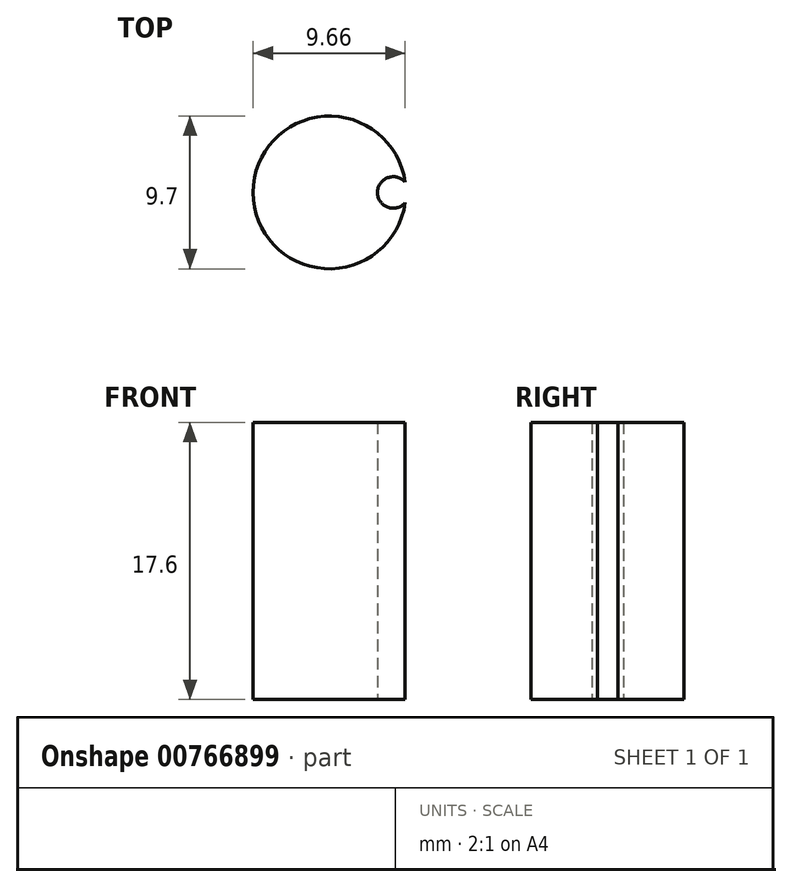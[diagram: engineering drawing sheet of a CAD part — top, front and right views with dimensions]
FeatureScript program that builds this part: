
annotation { "Feature Type Name" : "Feature", "Feature Type Description" : "" }
export const myFeature = defineFeature(function(context is Context, id is Id, definition is map)
    precondition{}
    {
        {
            var Q0;
            Q0=qCreatedBy(makeId("Top.planeOp"),FACE);
            var sketch = newSketch(context, id + "F0", { "sketchPlane" : qUnion([Q0])});
            skLineSegment(sketch, "E0", {"start": v(0, 0) * mm, "end": v(4.05, 0) * mm});
            skCircle(sketch, "E1", {"center": v(4.05, 0) * mm, "radius": 4.85 * mm});
            skLineSegment(sketch, "E2", {"start": v(0, 0) * mm, "end": v(0, -9.22) * mm});
            skCircle(sketch, "E3.MirrorC", {"center": v(-4.05, 0) * mm, "radius": 4.85 * mm});
            skCircle(sketch, "E4", {"center": v(0, 0) * mm, "radius": 1 * mm});
            skSolve(sketch);
        }
        {
            var Q0;
            {var subQ0=sQuery(id+"F0.wireOp",EDGE,"E3.MirrorC");var subQ1=sQuery(id+"F0.wireOp",EDGE,"E1");var subQ2=makeQuery(id+"F0.imprint","INTERSECT",VERTEX,{"derivedFrom":[subQ1,subQ0]});Q0=makeQuery(id+"F0.imprint","IMPRINT",FACE,{"disambiguationData":[TD([[makeQuery(id+"F0.imprint","IMPRINT",EDGE,{"disambiguationData":[TD([[subQ2,-1.0]])],"derivedFrom":subQ1}),-1.0]])]});}
            var Q1;
            {var subQ0=sQuery(id+"F0.wireOp",EDGE,"E3.MirrorC");var subQ1=sQuery(id+"F0.wireOp",EDGE,"E1");var subQ7=makeQuery(id+"F0.imprint","INTERSECT",VERTEX,{"derivedFrom":[subQ1,subQ0]});Q1=makeQuery(id+"F0.imprint","IMPRINT",FACE,{"disambiguationData":[TD([[makeQuery(id+"F0.imprint","IMPRINT",EDGE,{"disambiguationData":[TD([[subQ7,-1.0]])],"derivedFrom":subQ0}),1.0]])]});}
            var Q2;
            {var subQ1=sQuery(id+"F0.wireOp",EDGE,"E2");var subQ3=sQuery(id+"F0.wireOp",EDGE,"E4");var subQ4=makeQuery(id+"F0.imprint","INTERSECT",VERTEX,{"derivedFrom":[subQ1,subQ3]});Q2=makeQuery(id+"F0.imprint","IMPRINT",FACE,{"disambiguationData":[TD([[makeQuery(id+"F0.imprint","IMPRINT",EDGE,{"disambiguationData":[TD([[subQ4,-1.0]])],"derivedFrom":subQ3}),-1.0]])]});}
            var Q3;
            {var subQ0=sQuery(id+"F0.wireOp",EDGE,"E4");var subQ1=sQuery(id+"F0.wireOp",EDGE,"E1");var subQ2=makeQuery(id+"F0.imprint","INTERSECT",VERTEX,{"disambiguationData":[OD(1.0)],"derivedFrom":[subQ1,subQ0]});Q3=makeQuery(id+"F0.imprint","IMPRINT",FACE,{"disambiguationData":[TD([[makeQuery(id+"F0.imprint","IMPRINT",EDGE,{"disambiguationData":[TD([[subQ2,-1.0]])],"derivedFrom":subQ0}),-1.0]])]});}
            var Q4;
            {var subQ0=sQuery(id+"F0.wireOp",EDGE,"E3.MirrorC");var subQ1=sQuery(id+"F0.wireOp",EDGE,"E1");var subQ2=makeQuery(id+"F0.imprint","INTERSECT",VERTEX,{"derivedFrom":[subQ1,subQ0]});Q4=makeQuery(id+"F0.imprint","IMPRINT",FACE,{"disambiguationData":[TD([[makeQuery(id+"F0.imprint","IMPRINT",EDGE,{"disambiguationData":[TD([[subQ2,-1.0]])],"derivedFrom":subQ1}),1.0]])]});}
            extrude(context, id + "F1", {"entities" : qUnion([Q0, Q1, Q2, Q3, Q4]), "depth" : 17.6 * mm, "offsetDistance" : 25 * mm});
        }
    });
